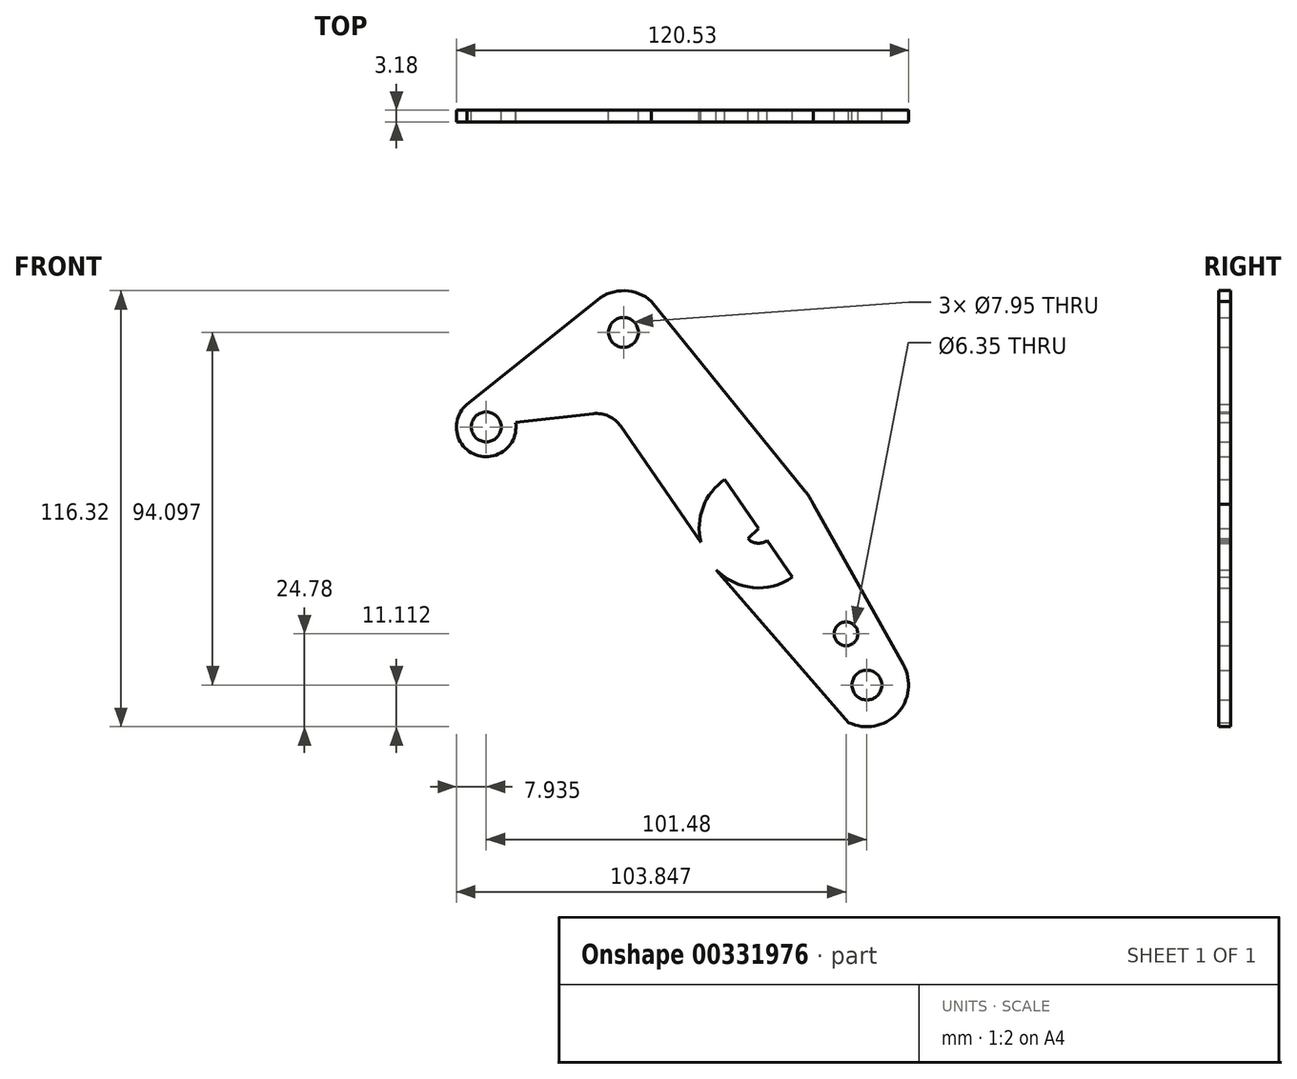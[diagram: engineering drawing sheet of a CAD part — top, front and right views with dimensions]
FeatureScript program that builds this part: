
annotation { "Feature Type Name" : "Feature", "Feature Type Description" : "" }
export const myFeature = defineFeature(function(context is Context, id is Id, definition is map)
    precondition{}
    {
        {
            var Q0;
            Q0=qCreatedBy(makeId("Front.planeOp"),FACE);
            var sketch = newSketch(context, id + "F0", { "sketchPlane" : qUnion([Q0])});
            skLineSegment(sketch, "E0", {"start": v(31.51, -43.2) * mm, "end": v(-33.37, 50.9) * mm});
            skLineSegment(sketch, "E1", {"start": v(-33.37, 50.9) * mm, "end": v(-69.96, 25.67) * mm});
            skLineSegment(sketch, "E2", {"start": v(-69.96, 25.67) * mm, "end": v(-69.96, -10.4) * mm});
            skLineSegment(sketch, "E3", {"start": v(-69.96, -10.4) * mm, "end": v(-42.86, -45.64) * mm});
            skLineSegment(sketch, "E4", {"start": v(-42.86, -45.64) * mm, "end": v(2.68, -1.38) * mm});
            skCircle(sketch, "E5", {"center": v(31.51, -43.2) * mm, "radius": 11.11 * mm});
            skCircle(sketch, "E6", {"center": v(2.68, -1.38) * mm, "radius": 15.88 * mm});
            skCircle(sketch, "E7", {"center": v(-33.37, 50.9) * mm, "radius": 11.11 * mm});
            skCircle(sketch, "E8", {"center": v(-69.96, 25.67) * mm, "radius": 7.94 * mm});
            skCircle(sketch, "E9", {"center": v(25.95, -29.53) * mm, "radius": 3.17 * mm});
            skCircle(sketch, "E10", {"center": v(-69.96, 25.67) * mm, "radius": 3.98 * mm});
            skCircle(sketch, "E11", {"center": v(-33.37, 50.9) * mm, "radius": 3.98 * mm});
            skCircle(sketch, "E12", {"center": v(2.68, -1.38) * mm, "radius": 3.98 * mm});
            skCircle(sketch, "E13", {"center": v(31.51, -43.2) * mm, "radius": 3.98 * mm});
            skCircle(sketch, "E14", {"center": v(-42.86, -45.64) * mm, "radius": 11.11 * mm});
            skCircle(sketch, "E15", {"center": v(-28.05, -31.24) * mm, "radius": 3.12 * mm});
            skCircle(sketch, "E16", {"center": v(-69.96, -10.4) * mm, "radius": 7.94 * mm});
            skCircle(sketch, "E17", {"center": v(-69.96, -10.4) * mm, "radius": 3.98 * mm});
            skCircle(sketch, "E18", {"center": v(-42.86, -45.64) * mm, "radius": 3.98 * mm});
            skLineSegment(sketch, "E19", {"start": v(-75.07, 31.74) * mm, "end": v(-40.32, 59.57) * mm});
            skLineSegment(sketch, "E20", {"start": v(-25.92, 59.14) * mm, "end": v(15.01, 8.62) * mm});
            skLineSegment(sketch, "E21", {"start": v(17.2, 5.05) * mm, "end": v(41.2, -37.76) * mm});
            skLineSegment(sketch, "E22", {"start": v(26.68, -53.2) * mm, "end": v(-8.72, -12.46) * mm});
            skLineSegment(sketch, "E23", {"start": v(-12.76, -5.09) * mm, "end": v(-34.07, 25.81) * mm});
            skLineSegment(sketch, "E24", {"start": v(-41.49, 29.2) * mm, "end": v(-62.13, 26.91) * mm});
            skPoint(sketch, "E25.visualSharp", {"position": v(-36.76, 29.72) * mm});
            skArc(sketch, "E25.filletArc", {"start": v(-34.07, 25.81) * mm, "mid": v(-37.3, 28.53) * mm, "end": v(-41.49, 29.2) * mm});
            skLineSegment(sketch, "E26", {"start": v(-47.02, -28.76) * mm, "end": v(-62.54, -7.6) * mm});
            skPoint(sketch, "E27.visualSharp", {"position": v(-43.38, -33.72) * mm});
            skArc(sketch, "E27.filletArc", {"start": v(-47.02, -28.76) * mm, "mid": v(-40.7, -32) * mm, "end": v(-34.3, -28.89) * mm});
            skLineSegment(sketch, "E28", {"start": v(-71.85, -18.12) * mm, "end": v(-52.45, -51.25) * mm});
            skLineSegment(sketch, "E29", {"start": v(-33.2, -51.15) * mm, "end": v(12.71, -13.68) * mm});
            skLineSegment(sketch, "E30", {"start": v(-34.3, -28.89) * mm, "end": v(-9.7, 8.58) * mm});
            skSolve(sketch);
        }
        {
            var Q0;
            {var subQ14=sQuery(id+"F0.wireOp",EDGE,"E24");Q0=makeQuery(id+"F0.imprint","IMPRINT",FACE,{"disambiguationData":[TD([[makeQuery(id+"F0.imprint","IMPRINT",EDGE,{"derivedFrom":subQ14}),-1.0]])]});}
            var Q1;
            {var subQ5=sQuery(id+"F0.wireOp",EDGE,"E19");Q1=makeQuery(id+"F0.imprint","IMPRINT",FACE,{"disambiguationData":[TD([[makeQuery(id+"F0.imprint","IMPRINT",EDGE,{"derivedFrom":subQ5}),-1.0]])]});}
            var Q2;
            {var subQ0=sQuery(id+"F0.wireOp",EDGE,"E8");var subQ6=sQuery(id+"F0.wireOp",EDGE,"E1");var subQ7=makeQuery(id+"F0.imprint","INTERSECT",VERTEX,{"derivedFrom":[subQ6,subQ0]});Q2=makeQuery(id+"F0.imprint","IMPRINT",FACE,{"disambiguationData":[TD([[makeQuery(id+"F0.imprint","IMPRINT",EDGE,{"disambiguationData":[TD([[subQ7,-1.0]])],"derivedFrom":subQ6}),1.0]])]});}
            var Q3;
            {var subQ0=sQuery(id+"F0.wireOp",EDGE,"E8");var subQ2=sQuery(id+"F0.wireOp",EDGE,"E1");var subQ3=makeQuery(id+"F0.imprint","INTERSECT",VERTEX,{"derivedFrom":[subQ2,subQ0]});Q3=makeQuery(id+"F0.imprint","IMPRINT",FACE,{"disambiguationData":[TD([[makeQuery(id+"F0.imprint","IMPRINT",EDGE,{"disambiguationData":[TD([[subQ3,-1.0]])],"derivedFrom":subQ2}),-1.0]])]});}
            var Q4;
            {var subQ0=sQuery(id+"F0.wireOp",EDGE,"E7");var subQ5=sQuery(id+"F0.wireOp",EDGE,"E0");var subQ11=makeQuery(id+"F0.imprint","INTERSECT",VERTEX,{"derivedFrom":[subQ5,subQ0]});Q4=makeQuery(id+"F0.imprint","IMPRINT",FACE,{"disambiguationData":[TD([[makeQuery(id+"F0.imprint","IMPRINT",EDGE,{"disambiguationData":[TD([[subQ11,-1.0]])],"derivedFrom":subQ5}),-1.0]])]});}
            var Q5;
            {var subQ0=sQuery(id+"F0.wireOp",EDGE,"E6");var subQ1=sQuery(id+"F0.wireOp",EDGE,"E0");var subQ2=makeQuery(id+"F0.imprint","INTERSECT",VERTEX,{"disambiguationData":[OD(1.0)],"derivedFrom":[subQ1,subQ0]});Q5=makeQuery(id+"F0.imprint","IMPRINT",FACE,{"disambiguationData":[TD([[makeQuery(id+"F0.imprint","IMPRINT",EDGE,{"disambiguationData":[TD([[subQ2,-1.0]])],"derivedFrom":subQ1}),-1.0]])]});}
            var Q6;
            {var subQ0=sQuery(id+"F0.wireOp",EDGE,"E7");var subQ1=sQuery(id+"F0.wireOp",EDGE,"E0");var subQ2=makeQuery(id+"F0.imprint","INTERSECT",VERTEX,{"derivedFrom":[subQ1,subQ0]});Q6=makeQuery(id+"F0.imprint","IMPRINT",FACE,{"disambiguationData":[TD([[makeQuery(id+"F0.imprint","IMPRINT",EDGE,{"disambiguationData":[TD([[subQ2,-1.0]])],"derivedFrom":subQ1}),1.0]])]});}
            var Q7;
            {var subQ0=sQuery(id+"F0.wireOp",EDGE,"E6");var subQ2=sQuery(id+"F0.wireOp",EDGE,"E0");var subQ5=makeQuery(id+"F0.imprint","INTERSECT",VERTEX,{"disambiguationData":[OD(0.0)],"derivedFrom":[subQ2,subQ0]});Q7=makeQuery(id+"F0.imprint","IMPRINT",FACE,{"disambiguationData":[TD([[makeQuery(id+"F0.imprint","IMPRINT",EDGE,{"disambiguationData":[TD([[subQ5,-1.0]])],"derivedFrom":subQ2}),-1.0]])]});}
            var Q8;
            {var subQ5=sQuery(id+"F0.wireOp",EDGE,"E0");var subQ9=sQuery(id+"F0.wireOp",EDGE,"E12");var subQ11=makeQuery(id+"F0.imprint","INTERSECT",VERTEX,{"disambiguationData":[OD(1.0)],"derivedFrom":[subQ5,subQ9]});Q8=makeQuery(id+"F0.imprint","IMPRINT",FACE,{"disambiguationData":[TD([[makeQuery(id+"F0.imprint","IMPRINT",EDGE,{"disambiguationData":[TD([[subQ11,-1.0]])],"derivedFrom":subQ5}),1.0]])]});}
            var Q9;
            {var subQ0=sQuery(id+"F0.wireOp",EDGE,"E23");var subQ1=sQuery(id+"F0.wireOp",EDGE,"E6");var subQ2=makeQuery(id+"F0.imprint","INTERSECT",VERTEX,{"derivedFrom":[subQ1,subQ0]});Q9=makeQuery(id+"F0.imprint","IMPRINT",FACE,{"disambiguationData":[TD([[makeQuery(id+"F0.imprint","IMPRINT",EDGE,{"disambiguationData":[TD([[subQ2,1.0]])],"derivedFrom":subQ1}),-1.0]])]});}
            var Q10;
            {var subQ0=sQuery(id+"F0.wireOp",EDGE,"E6");var subQ1=sQuery(id+"F0.wireOp",EDGE,"E0");var subQ2=makeQuery(id+"F0.imprint","INTERSECT",VERTEX,{"disambiguationData":[OD(0.0)],"derivedFrom":[subQ1,subQ0]});Q10=makeQuery(id+"F0.imprint","IMPRINT",FACE,{"disambiguationData":[TD([[makeQuery(id+"F0.imprint","IMPRINT",EDGE,{"disambiguationData":[TD([[subQ2,-1.0]])],"derivedFrom":subQ1}),1.0]])]});}
            var Q11;
            {var subQ3=sQuery(id+"F0.wireOp",EDGE,"E29");var subQ7=sQuery(id+"F0.wireOp",EDGE,"E0");var subQ8=makeQuery(id+"F0.imprint","INTERSECT",VERTEX,{"derivedFrom":[subQ7,subQ3]});Q11=makeQuery(id+"F0.imprint","IMPRINT",FACE,{"disambiguationData":[TD([[makeQuery(id+"F0.imprint","IMPRINT",EDGE,{"disambiguationData":[TD([[subQ8,-1.0]])],"derivedFrom":subQ7}),1.0]])]});}
            var Q12;
            {var subQ5=sQuery(id+"F0.wireOp",EDGE,"E0");var subQ7=makeQuery(id+"F0.imprint","INTERSECT",VERTEX,{"derivedFrom":[subQ5,sQuery(id+"F0.wireOp",EDGE,"E9")]});Q12=makeQuery(id+"F0.imprint","IMPRINT",FACE,{"disambiguationData":[TD([[makeQuery(id+"F0.imprint","IMPRINT",EDGE,{"disambiguationData":[TD([[subQ7,1.0]])],"derivedFrom":subQ5}),1.0]])]});}
            var Q13;
            {var subQ7=sQuery(id+"F0.wireOp",EDGE,"E9");Q13=makeQuery(id+"F0.imprint","IMPRINT",FACE,{"disambiguationData":[TD([[makeQuery(id+"F0.imprint","IMPRINT",EDGE,{"derivedFrom":subQ7}),-1.0]])]});}
            var Q14;
            Q14=makeQuery(id+"F0.imprint","IMPRINT",FACE,{"disambiguationData":[TD([[makeQuery(id+"F0.imprint","IMPRINT",EDGE,{"derivedFrom":sQuery(id+"F0.wireOp",EDGE,"E13")}),-1.0]])]});
            var Q15;
            {var subQ0=sQuery(id+"F0.wireOp",EDGE,"qt7VXa1t-CWqT-gJuH-Uatk-Ju1OBdlZslns");var subQ1=sQuery(id+"F0.wireOp",EDGE,"E0");var subQ2=makeQuery(id+"F0.imprint","INTERSECT",VERTEX,{"derivedFrom":[subQ1,subQ0]});Q15=makeQuery(id+"F0.imprint","IMPRINT",FACE,{"disambiguationData":[TD([[makeQuery(id+"F0.imprint","IMPRINT",EDGE,{"disambiguationData":[TD([[subQ2,-1.0]])],"derivedFrom":subQ1}),1.0]])]});}
            var Q16;
            {var subQ0=sQuery(id+"F0.wireOp",EDGE,"E29");var subQ1=sQuery(id+"F0.wireOp",EDGE,"E0");var subQ2=makeQuery(id+"F0.imprint","INTERSECT",VERTEX,{"derivedFrom":[subQ1,subQ0]});Q16=makeQuery(id+"F0.imprint","IMPRINT",FACE,{"disambiguationData":[TD([[makeQuery(id+"F0.imprint","IMPRINT",EDGE,{"disambiguationData":[TD([[subQ2,-1.0]])],"derivedFrom":subQ1}),-1.0]])]});}
            var Q17;
            {var subQ0=sQuery(id+"F0.wireOp",EDGE,"qt7VXa1t-CWqT-gJuH-Uatk-Ju1OBdlZslns");var subQ1=sQuery(id+"F0.wireOp",EDGE,"E0");var subQ2=makeQuery(id+"F0.imprint","INTERSECT",VERTEX,{"derivedFrom":[subQ1,subQ0]});Q17=makeQuery(id+"F0.imprint","IMPRINT",FACE,{"disambiguationData":[TD([[makeQuery(id+"F0.imprint","IMPRINT",EDGE,{"disambiguationData":[TD([[subQ2,-1.0]])],"derivedFrom":subQ1}),-1.0]])]});}
            extrude(context, id + "F1", {"entities" : qUnion([Q0, Q1, Q2, Q3, Q4, Q5, Q6, Q7, Q8, Q9, Q10, Q11, Q12, Q13, Q14, Q15, Q16, Q17]), "depth" : 3.17 * mm});
        }
    });
